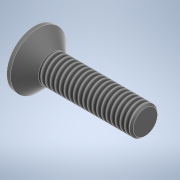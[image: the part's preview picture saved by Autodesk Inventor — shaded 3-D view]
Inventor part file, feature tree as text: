
AUTODESK INVENTOR PART (.ipt)
format: ipt  version: 2022 (Build 260153000, 153)  size: 130,560 bytes
history: native  units: mm
features: sketch x2, revolve x1, extrude x1, thread x1, chamfer x1
ambient origin geometry x8: Origin, YZ Plane, XZ Plane, XY Plane, X Axis, Y Axis, Z Axis, Center Point
bodies: Solid1 (feature_tree)
feature tree (6):
  revolve  "Revolution1"  Angle=45.0deg
  extrude  "Extrusion1"  Depth=1.5mm
  thread  "Thread1"  [1 undecoded]
  chamfer  "Chamfer1"  Angle=90.0deg  [1 undecoded]
  sketch  "Sketch1"  dims[d0=10.0mm d1=45.0deg]
  sketch  "Sketch2"  dims[d2=1.9mm d3=1.5mm d4=3.0mm d5=90.0deg d6=2.0mm d7=1.2mm d8=0.0mm d9=10.0mm d10=0.0mm d11=0.2mm d12=2.0mm d13=45.0deg]
note: 2 required parameter values undecoded (feature->parameter linkage not recoverable at this tier; creation-order binding heuristic only, values carry confidence <= 0.55)
